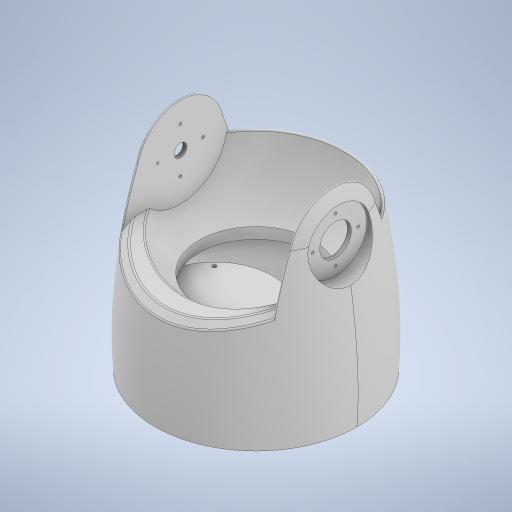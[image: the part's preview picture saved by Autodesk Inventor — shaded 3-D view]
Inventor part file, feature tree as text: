
AUTODESK INVENTOR PART (.ipt)
format: ipt  version: 2023.1 (Build 271208000, 208)  size: 814,592 bytes
history: native  units: mm
features: sketch x15, extrude x14, fillet x4, other x3, revolve x3, chamfer x3, mirror x2, projected_geometry x2, pattern_circular x1
ambient origin geometry x8: Origin, YZ Plane, XZ Plane, XY Plane, X Axis, Y Axis, Z Axis, Center Point
bodies: Body1 (feature_tree)
feature tree (47):
  other  "솔리드1"
  revolve  "회전1"
  sketch  "스케치2"
  revolve  "회전2"
  revolve  "회전3"
  extrude  "돌출3"  Depth=120.0mm
  extrude  "돌출4"  Depth=140.0mm
  chamfer  "모따기1"  Distance=60.0mm
  fillet  "모깎기1"  Radius=130.0mm
  extrude  "돌출5"  Depth=160.0mm
  fillet  "모깎기2"  [1 undecoded]
  fillet  "모깎기3"  Radius=120.0mm
  extrude  "돌출6"  Depth=141.0mm
  other  "작업 평면2"
  extrude  "돌출7"  TaperAngle=90.0deg  [1 undecoded]
  mirror  "미러1"
  extrude  "돌출9"  Depth=4.0mm
  extrude  "돌출10"  TaperAngle=90.0deg  [1 undecoded]
  mirror  "미러2"
  sketch  "스케치13"
  extrude  "돌출11"  Depth=10.0mm
  extrude  "돌출12"  Depth=371.75mm TaperAngle=0.0deg
  sketch  "스케치15"
  extrude  "돌출13"  Depth=25.0mm
  extrude  "돌출14"  Depth=140.0mm
  pattern_circular  "원형 패턴1"  [2 undecoded]
  extrude  "돌출15"  Depth=103.5mm TaperAngle=0.0deg
  fillet  "모깎기4"  Radius=5.0mm
  other  "작업 평면4"
  extrude  "돌출16"  Depth=2.0mm
  chamfer  "모따기2"  Distance=90.0mm
  extrude  "돌출17"  Depth=103.5mm TaperAngle=0.0deg
  chamfer  "모따기3"  Distance=1.0mm
  sketch  "스케치1"
  sketch  "스케치3"
  projected_geometry  "투영된 루프1"
  sketch  "스케치5"
  sketch  "스케치6"
  sketch  "스케치7"
  sketch  "스케치8"
  projected_geometry  "투영된 루프2"
  sketch  "스케치9"
  sketch  "스케치11"
  sketch  "스케치12"
  sketch  "스케치16"
  sketch  "스케치17"
  sketch  "스케치18"
note: 5 required parameter values undecoded (feature->parameter linkage not recoverable at this tier; creation-order binding heuristic only, values carry confidence <= 0.55)
